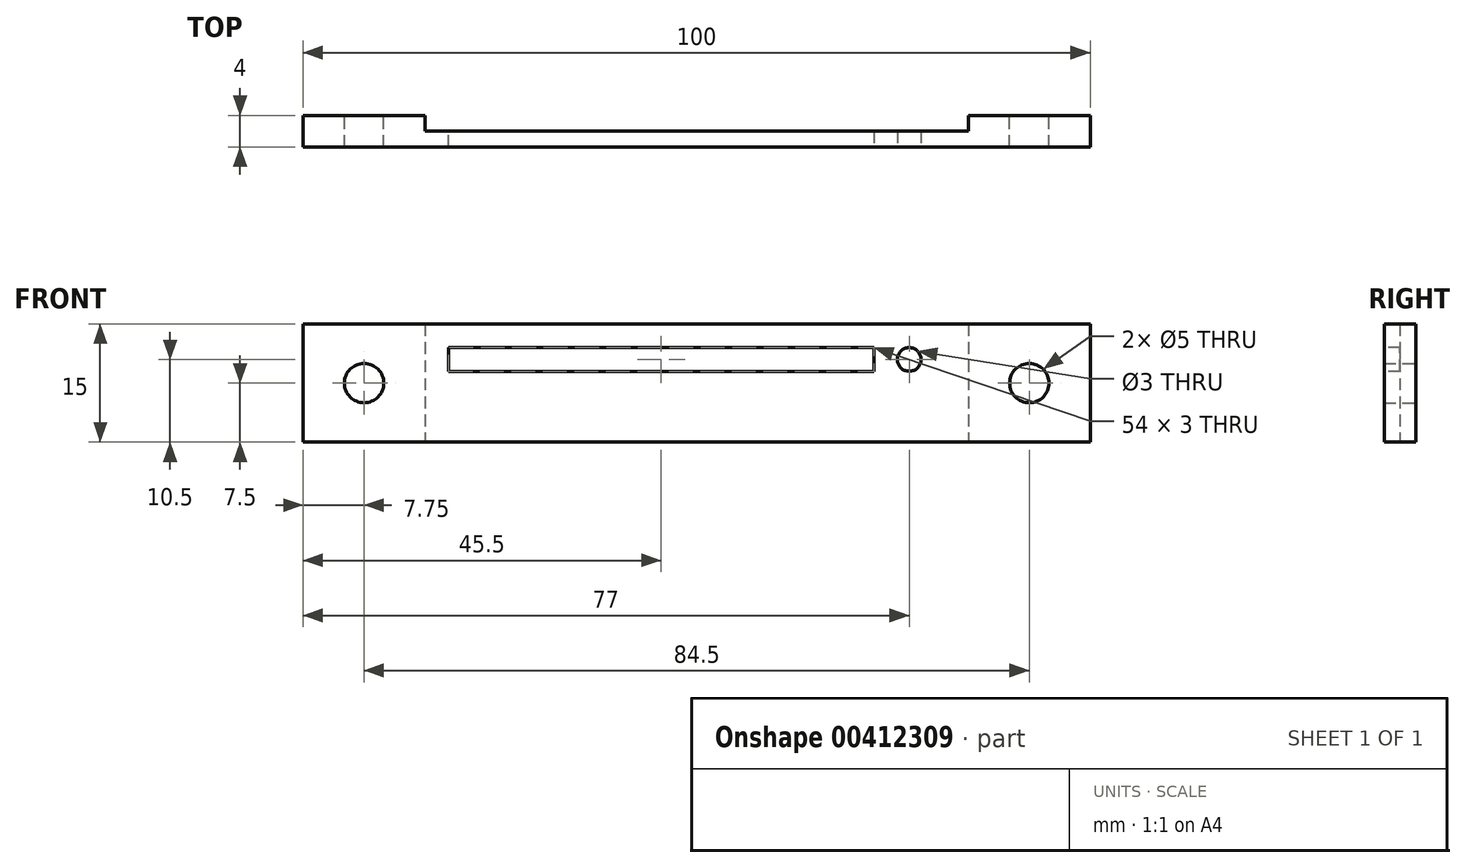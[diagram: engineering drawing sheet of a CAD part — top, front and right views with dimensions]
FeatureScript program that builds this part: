
annotation { "Feature Type Name" : "Feature", "Feature Type Description" : "" }
export const myFeature = defineFeature(function(context is Context, id is Id, definition is map)
    precondition{}
    {
        {
            var Q0;
            Q0=qCreatedBy(makeId("Front.planeOp"),FACE);
            var sketch = newSketch(context, id + "F0", { "sketchPlane" : qUnion([Q0])});
            skLineSegment(sketch, "E0.bottom", {"start": v(50, 7.5) * mm, "end": v(-50, 7.5) * mm});
            skLineSegment(sketch, "E0.top", {"start": v(50, -7.5) * mm, "end": v(-50, -7.5) * mm});
            skLineSegment(sketch, "E0.left", {"start": v(50, 7.5) * mm, "end": v(50, -7.5) * mm});
            skLineSegment(sketch, "E0.right", {"start": v(-50, 7.5) * mm, "end": v(-50, -7.5) * mm});
            skPoint(sketch, "E0.middle", {"position": v(0, 0) * mm});
            skLineSegment(sketch, "E1.bottom", {"start": v(31.5, 4.5) * mm, "end": v(-31.5, 4.5) * mm});
            skLineSegment(sketch, "E1.top", {"start": v(31.5, 1.5) * mm, "end": v(-31.5, 1.5) * mm});
            skLineSegment(sketch, "E1.left", {"start": v(31.5, 4.5) * mm, "end": v(31.5, 1.5) * mm});
            skLineSegment(sketch, "E1.right", {"start": v(-31.5, 4.5) * mm, "end": v(-31.5, 1.5) * mm});
            skPoint(sketch, "E1.middle", {"position": v(0, 3) * mm});
            skLineSegment(sketch, "E2.bottom", {"start": v(31.5, -1.5) * mm, "end": v(-31.5, -1.5) * mm});
            skLineSegment(sketch, "E2.top", {"start": v(31.5, -4.5) * mm, "end": v(-31.5, -4.5) * mm});
            skLineSegment(sketch, "E2.left", {"start": v(31.5, -1.5) * mm, "end": v(31.5, -4.5) * mm});
            skLineSegment(sketch, "E2.right", {"start": v(-31.5, -1.5) * mm, "end": v(-31.5, -4.5) * mm});
            skPoint(sketch, "E2.middle", {"position": v(0, -3) * mm});
            skSolve(sketch);
        }
        {
            var Q0;
            Q0=qSketchRegion(id+"F0",true);
            extrude(context, id + "F1", {"entities" : qUnion([Q0]), "depth" : 4 * mm});
        }
        {
            var Q0;
            Q0=makeQuery(id+"F1.opExtrude","CAP_FACE",FACE,{"disambiguationData":[OSD([sQuery(id+"F0.wireOp",EDGE,"E0.bottom"),sQuery(id+"F0.wireOp",EDGE,"E0.top"),sQuery(id+"F0.wireOp",EDGE,"E0.left"),sQuery(id+"F0.wireOp",EDGE,"E0.right"),sQuery(id+"F0.wireOp",EDGE,"E1.bottom"),sQuery(id+"F0.wireOp",EDGE,"E1.top"),sQuery(id+"F0.wireOp",EDGE,"E1.left"),sQuery(id+"F0.wireOp",EDGE,"E1.right"),sQuery(id+"F0.wireOp",EDGE,"E2.bottom"),sQuery(id+"F0.wireOp",EDGE,"E2.top"),sQuery(id+"F0.wireOp",EDGE,"E2.left"),sQuery(id+"F0.wireOp",EDGE,"E2.right")])],"isStart":true});
            var sketch = newSketch(context, id + "F2", { "sketchPlane" : qUnion([Q0])});
            skLineSegment(sketch, "E3.bottom", {"start": v(34.5, 7.5) * mm, "end": v(-34.5, 7.5) * mm});
            skLineSegment(sketch, "E3.top", {"start": v(34.5, -7.5) * mm, "end": v(-34.5, -7.5) * mm});
            skLineSegment(sketch, "E3.left", {"start": v(34.5, 7.5) * mm, "end": v(34.5, -7.5) * mm});
            skLineSegment(sketch, "E3.right", {"start": v(-34.5, 7.5) * mm, "end": v(-34.5, -7.5) * mm});
            skPoint(sketch, "E3.middle", {"position": v(0, 0) * mm});
            skSolve(sketch);
        }
        {
            var Q0;
            Q0=qSketchRegion(id+"F2",true);
            extrude(context, id + "F3", {"entities" : qUnion([Q0]), "operationType" : NewBodyOperationType.REMOVE, "oppositeDirection" : true, "depth" : 2 * mm});
        }
        {
            var Q0;
            {var subQ0=sQuery(id+"F0.wireOp",EDGE,"E0.bottom");var subQ1=sQuery(id+"F0.wireOp",EDGE,"E0.top");var subQ2=sQuery(id+"F0.wireOp",EDGE,"E0.left");Q0=makeQuery(id+"F3.boolean.opBoolean","SPLIT",FACE,{"disambiguationData":[TD([makeQuery(id+"F1.opExtrude","SWEPT_FACE",FACE,{"disambiguationData":[OSD([subQ2])]})])],"derivedFrom":makeQuery(id+"F1.opExtrude","CAP_FACE",FACE,{"disambiguationData":[OSD([subQ0,subQ1,subQ2,sQuery(id+"F0.wireOp",EDGE,"E0.right"),sQuery(id+"F0.wireOp",EDGE,"E1.bottom"),sQuery(id+"F0.wireOp",EDGE,"E1.top"),sQuery(id+"F0.wireOp",EDGE,"E1.left"),sQuery(id+"F0.wireOp",EDGE,"E1.right"),sQuery(id+"F0.wireOp",EDGE,"E2.bottom"),sQuery(id+"F0.wireOp",EDGE,"E2.top"),sQuery(id+"F0.wireOp",EDGE,"E2.left"),sQuery(id+"F0.wireOp",EDGE,"E2.right")])],"isStart":true})});}
            var sketch = newSketch(context, id + "F4", { "sketchPlane" : qUnion([Q0])});
            skLineSegment(sketch, "E4", {"start": v(-34.5, 7.5) * mm, "end": v(-50, -7.5) * mm, "construction": true});
            skLineSegment(sketch, "E5", {"start": v(-50, -7.5) * mm, "end": v(-50, 7.5) * mm, "construction": true});
            skLineSegment(sketch, "E6", {"start": v(-50, 7.5) * mm, "end": v(-34.5, -7.5) * mm, "construction": true});
            skCircle(sketch, "E7", {"center": v(-42.25, 0) * mm, "radius": 2.5 * mm});
            skSolve(sketch);
        }
        {
            var Q0;
            Q0=qSketchRegion(id+"F4",true);
            extrude(context, id + "F5", {"entities" : qUnion([Q0]), "operationType" : NewBodyOperationType.REMOVE, "oppositeDirection" : true, "depth" : 25 * mm});
        }
        {
            var Q0;
            {var subQ0=sQuery(id+"F0.wireOp",EDGE,"E0.bottom");var subQ1=sQuery(id+"F0.wireOp",EDGE,"E0.right");var subQ2=sQuery(id+"F0.wireOp",EDGE,"E0.top");Q0=makeQuery(id+"F3.boolean.opBoolean","SPLIT",FACE,{"disambiguationData":[TD([makeQuery(id+"F1.opExtrude","SWEPT_FACE",FACE,{"disambiguationData":[OSD([subQ1])]})])],"derivedFrom":makeQuery(id+"F1.opExtrude","CAP_FACE",FACE,{"disambiguationData":[OSD([subQ0,subQ2,sQuery(id+"F0.wireOp",EDGE,"E0.left"),subQ1,sQuery(id+"F0.wireOp",EDGE,"E1.bottom"),sQuery(id+"F0.wireOp",EDGE,"E1.top"),sQuery(id+"F0.wireOp",EDGE,"E1.left"),sQuery(id+"F0.wireOp",EDGE,"E1.right"),sQuery(id+"F0.wireOp",EDGE,"E2.bottom"),sQuery(id+"F0.wireOp",EDGE,"E2.top"),sQuery(id+"F0.wireOp",EDGE,"E2.left"),sQuery(id+"F0.wireOp",EDGE,"E2.right")])],"isStart":true})});}
            var sketch = newSketch(context, id + "F6", { "sketchPlane" : qUnion([Q0])});
            skLineSegment(sketch, "E8", {"start": v(34.5, 7.5) * mm, "end": v(50, -7.5) * mm, "construction": true});
            skCircle(sketch, "E9", {"center": v(42.25, 0) * mm, "radius": 2.5 * mm});
            skSolve(sketch);
        }
        {
            var Q0;
            Q0=qSketchRegion(id+"F6",true);
            extrude(context, id + "F7", {"entities" : qUnion([Q0]), "operationType" : NewBodyOperationType.REMOVE, "oppositeDirection" : true, "depth" : 25 * mm});
        }
        {
            var Q0;
            Q0=makeQuery(id+"F1.opExtrude","CAP_FACE",FACE,{"disambiguationData":[OSD([sQuery(id+"F0.wireOp",EDGE,"E0.bottom"),sQuery(id+"F0.wireOp",EDGE,"E0.top"),sQuery(id+"F0.wireOp",EDGE,"E0.left"),sQuery(id+"F0.wireOp",EDGE,"E0.right"),sQuery(id+"F0.wireOp",EDGE,"E1.bottom"),sQuery(id+"F0.wireOp",EDGE,"E1.top"),sQuery(id+"F0.wireOp",EDGE,"E1.left"),sQuery(id+"F0.wireOp",EDGE,"E1.right"),sQuery(id+"F0.wireOp",EDGE,"E2.bottom"),sQuery(id+"F0.wireOp",EDGE,"E2.top"),sQuery(id+"F0.wireOp",EDGE,"E2.left"),sQuery(id+"F0.wireOp",EDGE,"E2.right")])],"isStart":false});
            var sketch = newSketch(context, id + "F8", { "sketchPlane" : qUnion([Q0])});
            skLineSegment(sketch, "E10.bottom", {"start": v(31.5, 4.5) * mm, "end": v(22.5, 4.5) * mm});
            skLineSegment(sketch, "E10.top", {"start": v(31.5, 1.5) * mm, "end": v(22.5, 1.5) * mm});
            skLineSegment(sketch, "E10.left", {"start": v(31.5, 4.5) * mm, "end": v(31.5, 1.5) * mm});
            skLineSegment(sketch, "E10.right", {"start": v(22.5, 4.5) * mm, "end": v(22.5, 1.5) * mm});
            skSolve(sketch);
        }
        {
            var Q0;
            Q0=qSketchRegion(id+"F8",true);
            extrude(context, id + "F9", {"entities" : qUnion([Q0]), "operationType" : NewBodyOperationType.ADD, "oppositeDirection" : true, "depth" : 2 * mm});
        }
        {
            var Q0;
            Q0=makeQuery(id+"F9.boolean.opBoolean","MERGE",FACE,{"derivedFrom":[makeQuery(id+"F1.opExtrude","CAP_FACE",FACE,{"disambiguationData":[OSD([sQuery(id+"F0.wireOp",EDGE,"E0.bottom"),sQuery(id+"F0.wireOp",EDGE,"E0.top"),sQuery(id+"F0.wireOp",EDGE,"E0.left"),sQuery(id+"F0.wireOp",EDGE,"E0.right"),sQuery(id+"F0.wireOp",EDGE,"E1.bottom"),sQuery(id+"F0.wireOp",EDGE,"E1.top"),sQuery(id+"F0.wireOp",EDGE,"E1.left"),sQuery(id+"F0.wireOp",EDGE,"E1.right"),sQuery(id+"F0.wireOp",EDGE,"E2.bottom"),sQuery(id+"F0.wireOp",EDGE,"E2.top"),sQuery(id+"F0.wireOp",EDGE,"E2.left"),sQuery(id+"F0.wireOp",EDGE,"E2.right")])],"isStart":false}),makeQuery(id+"F9.opExtrude","CAP_FACE",FACE,{"disambiguationData":[OSD([sQuery(id+"F8.wireOp",EDGE,"E10.bottom"),sQuery(id+"F8.wireOp",EDGE,"E10.top"),sQuery(id+"F8.wireOp",EDGE,"E10.left"),sQuery(id+"F8.wireOp",EDGE,"E10.right")])],"isStart":true})]});
            var sketch = newSketch(context, id + "F10", { "sketchPlane" : qUnion([Q0])});
            skCircle(sketch, "E11", {"center": v(27, 3) * mm, "radius": 1.5 * mm});
            skSolve(sketch);
        }
        {
            var Q0;
            Q0=qSketchRegion(id+"F10",true);
            extrude(context, id + "F11", {"entities" : qUnion([Q0]), "operationType" : NewBodyOperationType.REMOVE, "oppositeDirection" : true, "depth" : 25 * mm});
        }
        {
            var Q0;
            Q0=makeQuery(id+"F9.boolean.opBoolean","MERGE",FACE,{"derivedFrom":[makeQuery(id+"F1.opExtrude","CAP_FACE",FACE,{"disambiguationData":[OSD([sQuery(id+"F0.wireOp",EDGE,"E0.bottom"),sQuery(id+"F0.wireOp",EDGE,"E0.top"),sQuery(id+"F0.wireOp",EDGE,"E0.left"),sQuery(id+"F0.wireOp",EDGE,"E0.right"),sQuery(id+"F0.wireOp",EDGE,"E1.bottom"),sQuery(id+"F0.wireOp",EDGE,"E1.top"),sQuery(id+"F0.wireOp",EDGE,"E1.left"),sQuery(id+"F0.wireOp",EDGE,"E1.right"),sQuery(id+"F0.wireOp",EDGE,"E2.bottom"),sQuery(id+"F0.wireOp",EDGE,"E2.top"),sQuery(id+"F0.wireOp",EDGE,"E2.left"),sQuery(id+"F0.wireOp",EDGE,"E2.right")])],"isStart":false}),makeQuery(id+"F9.opExtrude","CAP_FACE",FACE,{"disambiguationData":[OSD([sQuery(id+"F8.wireOp",EDGE,"E10.bottom"),sQuery(id+"F8.wireOp",EDGE,"E10.top"),sQuery(id+"F8.wireOp",EDGE,"E10.left"),sQuery(id+"F8.wireOp",EDGE,"E10.right")])],"isStart":true})]});
            var sketch = newSketch(context, id + "F12", { "sketchPlane" : qUnion([Q0])});
            skLineSegment(sketch, "E12.bottom", {"start": v(-33.93, 0) * mm, "end": v(34.95, 0) * mm});
            skLineSegment(sketch, "E12.top", {"start": v(-33.93, -7.5) * mm, "end": v(34.95, -7.5) * mm});
            skLineSegment(sketch, "E12.left", {"start": v(-33.93, 0) * mm, "end": v(-33.93, -7.5) * mm});
            skLineSegment(sketch, "E12.right", {"start": v(34.95, 0) * mm, "end": v(34.95, -7.5) * mm});
            skSolve(sketch);
        }
        {
            var Q0;
            Q0 = qSketchRegion(id + "F12", true);
            extrude(context, id + "F13", {"entities" : qUnion([Q0]), "operationType" : NewBodyOperationType.ADD, "oppositeDirection" : true, "depth" : 2 * mm});
        }
    });
